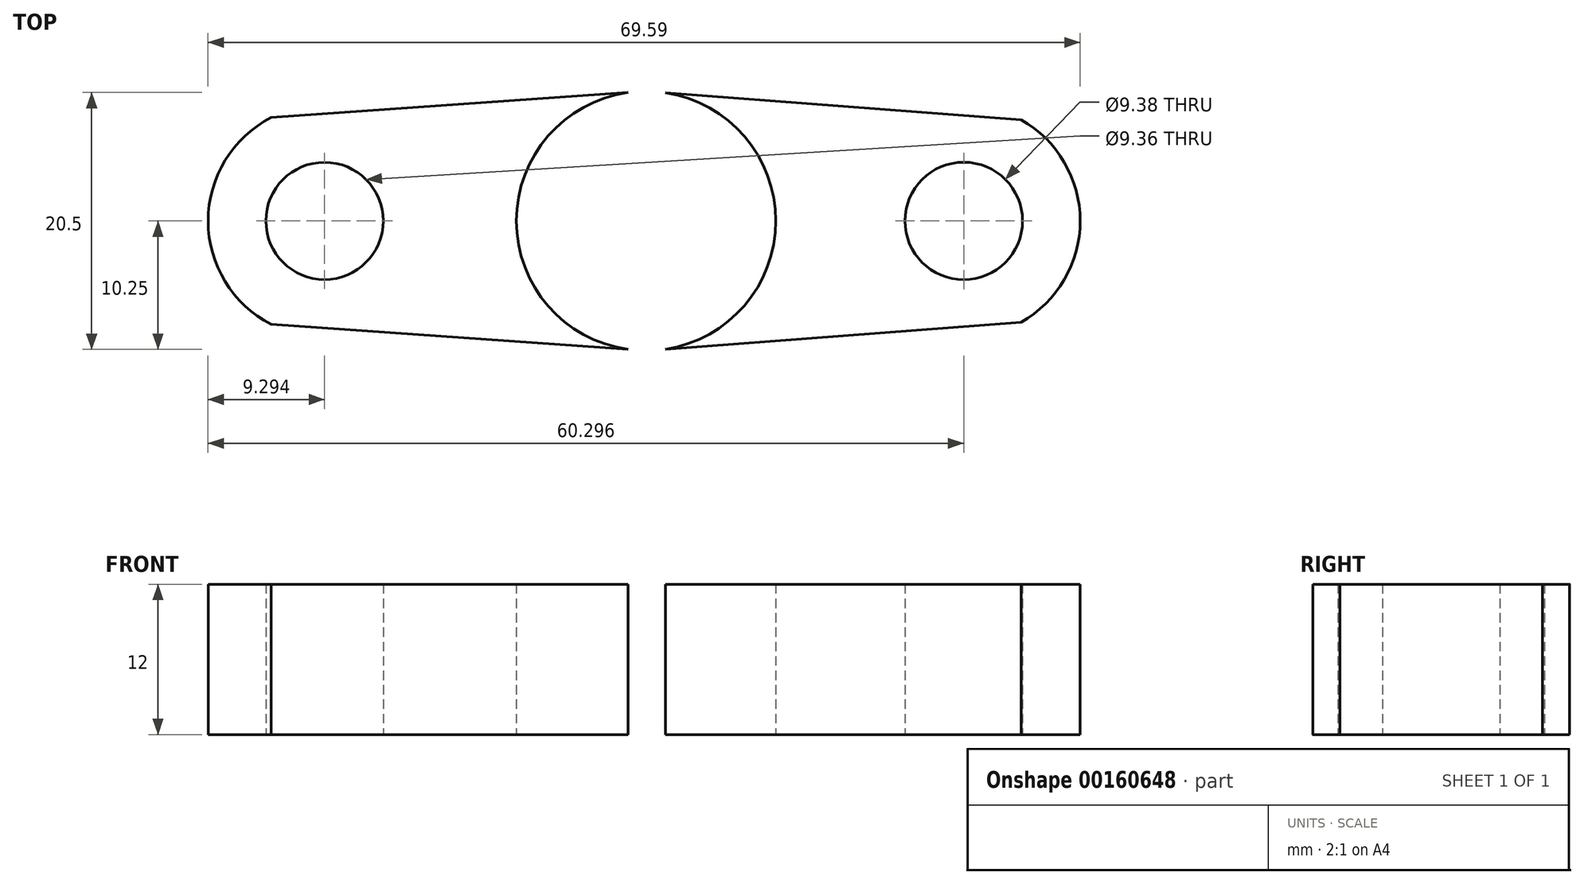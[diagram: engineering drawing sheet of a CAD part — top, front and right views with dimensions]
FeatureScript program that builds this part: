
annotation { "Feature Type Name" : "Feature", "Feature Type Description" : "" }
export const myFeature = defineFeature(function(context is Context, id is Id, definition is map)
    precondition{}
    {
        {
            var Q0;
            Q0=qCreatedBy(makeId("Top.planeOp"),FACE);
            var sketch = newSketch(context, id + "F0", { "sketchPlane" : qUnion([Q0])});
            skArc(sketch, "E0", {"start": v(0, 10.35) * mm, "mid": v(-10.35, 0) * mm, "end": v(0, -10.35) * mm});
            skArc(sketch, "E1", {"start": v(-29.93, 8.25) * mm, "mid": v(-34.95, 0) * mm, "end": v(-29.93, -8.25) * mm});
            skLineSegment(sketch, "E2", {"start": v(-29.93, 8.25) * mm, "end": v(0, 10.35) * mm});
            skLineSegment(sketch, "E3", {"start": v(-29.93, -8.25) * mm, "end": v(0, -10.35) * mm});
            skCircle(sketch, "E4", {"center": v(-25.66, 0) * mm, "radius": 4.68 * mm});
            skSolve(sketch);
        }
        {
            var Q0;
            {var subQ1=sQuery(id+"F0.wireOp",EDGE,"E1");Q0=makeQuery(id+"F0.imprint","IMPRINT",FACE,{"disambiguationData":[TD([[makeQuery(id+"F0.imprint","IMPRINT",EDGE,{"derivedFrom":subQ1}),1.0]])]});}
            extrude(context, id + "F1", {"entities" : qUnion([Q0]), "depth" : 12 * mm});
        }
        {
            var Q0;
            Q0=qCreatedBy(makeId("Top.planeOp"),FACE);
            var sketch = newSketch(context, id + "F2", { "sketchPlane" : qUnion([Q0])});
            skArc(sketch, "E5", {"start": v(0, -10.35) * mm, "mid": v(10.35, 0) * mm, "end": v(0, 10.35) * mm});
            skArc(sketch, "E6", {"start": v(29.91, -8.09) * mm, "mid": v(34.64, 0) * mm, "end": v(29.91, 8.09) * mm});
            skLineSegment(sketch, "E7", {"start": v(0, -10.35) * mm, "end": v(29.91, -8.09) * mm});
            skLineSegment(sketch, "E8", {"start": v(0, 10.35) * mm, "end": v(29.91, 8.09) * mm});
            skCircle(sketch, "E9", {"center": v(25.35, 0) * mm, "radius": 4.69 * mm});
            skSolve(sketch);
        }
        {
            var Q0;
            {var subQ1=sQuery(id+"F2.wireOp",EDGE,"E6");Q0=makeQuery(id+"F2.imprint","IMPRINT",FACE,{"disambiguationData":[TD([[makeQuery(id+"F2.imprint","IMPRINT",EDGE,{"derivedFrom":subQ1}),1.0]])]});}
            extrude(context, id + "F3", {"entities" : qUnion([Q0]), "depth" : 12 * mm});
        }
    });
